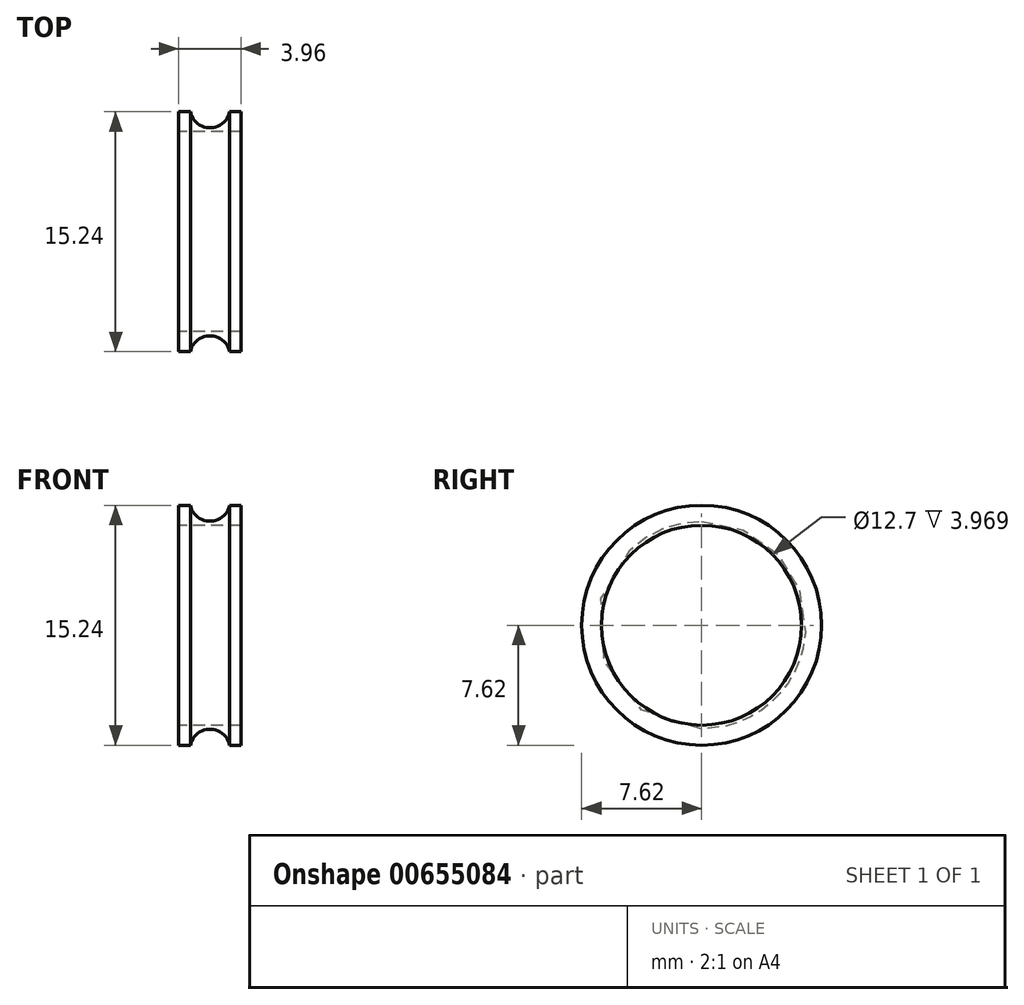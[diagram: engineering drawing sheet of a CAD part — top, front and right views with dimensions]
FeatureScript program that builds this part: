
annotation { "Feature Type Name" : "Feature", "Feature Type Description" : "" }
export const myFeature = defineFeature(function(context is Context, id is Id, definition is map)
    precondition{}
    {
        {
            var Q0;
            Q0=qCreatedBy(makeId("Front.planeOp"),FACE);
            var sketch = newSketch(context, id + "F0", { "sketchPlane" : qUnion([Q0])});
            skLineSegment(sketch, "E0.top", {"start": v(-1.98, 6.35) * mm, "end": v(1.98, 6.35) * mm});
            skLineSegment(sketch, "E0.left", {"start": v(-1.98, 7.62) * mm, "end": v(-1.98, 6.35) * mm});
            skLineSegment(sketch, "E0.right", {"start": v(1.98, 7.62) * mm, "end": v(1.98, 6.35) * mm});
            skLineSegment(sketch, "E1", {"start": v(-7.02, 0) * mm, "end": v(9.57, 0) * mm});
            skLineSegment(sketch, "E2", {"start": v(-1.98, 7.62) * mm, "end": v(-1.24, 7.62) * mm});
            skArc(sketch, "E3", {"start": v(-1.24, 7.62) * mm, "mid": v(0, 6.6) * mm, "end": v(1.24, 7.62) * mm});
            skLineSegment(sketch, "E4.trimOffspring", {"start": v(1.24, 7.62) * mm, "end": v(1.98, 7.62) * mm});
            skSolve(sketch);
        }
        {
            var Q0;
            Q0 = qSketchRegion(id + "F0", true);
            var Q1;
            Q1=sQuery(id+"F0.wireOp",EDGE,"E1");
            revolve(context, id + "F1", {"entities" : qUnion([Q0]), "axis" : qUnion([Q1]), "revolveType" : RevolveType.FULL});
        }
    });
